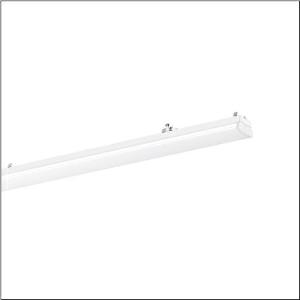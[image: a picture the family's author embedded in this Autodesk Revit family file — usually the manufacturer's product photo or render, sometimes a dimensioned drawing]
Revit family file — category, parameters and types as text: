
# Revit family: licross_r__11_recessed_opal_ho_51tl1ddn4d5m_587a
name_source: partatom
category: Lighting Fixtures
units: mm (PartAtom-declared; Revit-internal decimal feet)

## family parameters
Cut with Voids When Loaded = No
Host = Face
Light Source = No
Part Type = Normal
Room Calculation Point = No
Round Connector Dimension = Use Diameter
Shared = No

## types (1)
- --- (1 x LED, 13620 lm, 76.8 W, 4000K)
    Apparent Load = 77 VA
    CIE Flux Codes = 44 73 91 87 100
    Color Rendering = 80
    Color Temperature = 4000K
    Default Elevation = 1800 mm
    Description = Licross® 11 recessed opal HO, luminaire insert, of sheet steel, coil coated, white, length: 1.500mm, width: 76mm, height: 87mm, LED rated luminous flux: 13.620lm, light colour: 840, control gear: DALI 2, with plug, 5-pole, with phase selection, mains connection: 220..240V, AC, 50/60Hz, rated input power: 77W, halogen-free wiring, primary optical cover: cover, of PMMA, light emission: direct with ceiling illumination distribution, primary light characteristic: symmetric, protection rating (complete): IP40, insulation class (complete): insulation class I (protective earthing), certification: CE, ENEC, VDE, UKCA, protection symbol: D if used in an environment without relevant dust loads with corresponding accessories, impact resistance: IK06, permissible ambient temperature for indoor applications: -25..+30°C, corresponds to IFS (International Featured Standards) requirements for safety and quality in the food industry, reducing of maximum allowable ambient temperature of 5°C with ceiling mounting, LABS conformity tested according to VDMA 24364:2018-05, packaging unit: 1 piece
    Height = 83 mm
    Lamp = 1 x LED
    Lamp Light Flux = 13620 lm
    Lamp Power = 76.8 W
    Lamp count = 1
    Length = 1500 mm
    Luminous efficacy = 177 lm/W
    Manufacturer = Siteco
    ModVariant = No
    Model = 51TL1DDN4D5M
    Mounting Place = Ceiling
    Mounting Type = Pendant
    Number of Poles = 1
    OnlyDefault = Yes
    Power Factor = 1
    Product Name = Licross® 11 recessed opal HO
    Product group = luminaire insert
    ProductGroupID = 901
    Protection Class = Protection class I
    Protection Degree = IP 40
    RLX_Detail_Level = 1
    RLX_Emergency_Light_Flux = 0 lm
    RLX_Emergency_Type = 0
    RLX_Emergency_Type_DB = No
    RlxData = <blob elided: 26841 chars, md5=b585f768>
    Socket = socket
    Standby Power = 0 W
    System Light Flux = 13620 lm
    System Power = 77 W
    Type Comments = factory setting: luminous flux: 100 % | dim-lin: 254 | 522 mA
    Type Image = l_1313666.jpg
    URL = http://relux.com
    VarID = @adj_045045
    Voltage = 0 V
    Weight = 0.00 kg
    Width = 76 mm

## geometry (parser evidence)
native form markers: Blend x4, Sweep x14
no freeform markers — native parametric forms only
